# Revit family: STH21951BR_27_STH21951PTO_27
name_source: partatom
category: Luminárias
units: mm (PartAtom-declared; Revit-internal decimal feet)

## family parameters
Compartilhado = Não
Corte com vazios quando carregada = Não
Cota do conector redondo = Utilizar diâmetro
Fonte luminosa = Sim
Hospedeiro = Forro
Manter orientação da anotação = Não
Número OmniClass = 23.80.70.11
Ponto de cálculo do ambiente = Não
Sempre na vertical = Sim
Tipo de parte = Normal
Título OmniClass = Luminaries for Internal Lighting

## types (2) — shared parameters
Altura = 0.01 m
Comprimento = 1.02 m
Dimerização = Não dimerizável
Fabricante = Stella
Filtro de cor = 16777215
Grau de proteção (IP) = IP20
IRC (Índice de reprodução de cores) = >93 (R9 >60)
Largura = 0.02 m
Luminoso = Luminoso - 2700K
Modelo = Archi
Potência = 5 W
Temperatura da cor (K) = 2700 K
Tensão Elétrica = 24V
Troca de temperatura da cor de lâmpada com esmaecimento = <Nenhum>
URL = https://stella.com.br
Ângulo de Abertura = 110°
Ângulo de inclinação = 90.00°
zero-valued in all types: Elevação padrão

## per-type parameters (varying)
| type | Arquivo de rede fotométrica | Estrutura | Fluxo Luminoso | Referência |
| STH21951BR/27 - BRANCO - 1m - 2700K - 220lm - 110° | STELLA - STH21951BR-27 - ARCHI - PERFIL DE EMBUTIR PLANO 16mm.ies | Al - Branco | 220 lm | STH21951BR/27 - BRANCO - 1m |
| STH21951PTO/27 - PRETO - 1m - 2700K - 110lm - 110° | STELLA - STH21951PTO-27 - ARCHI - PERFIL DE EMBUTIR PLANO 16mm.ies | Al - Preto | 110 lm | STH21951PTO/27 - PRETO - 1m |
